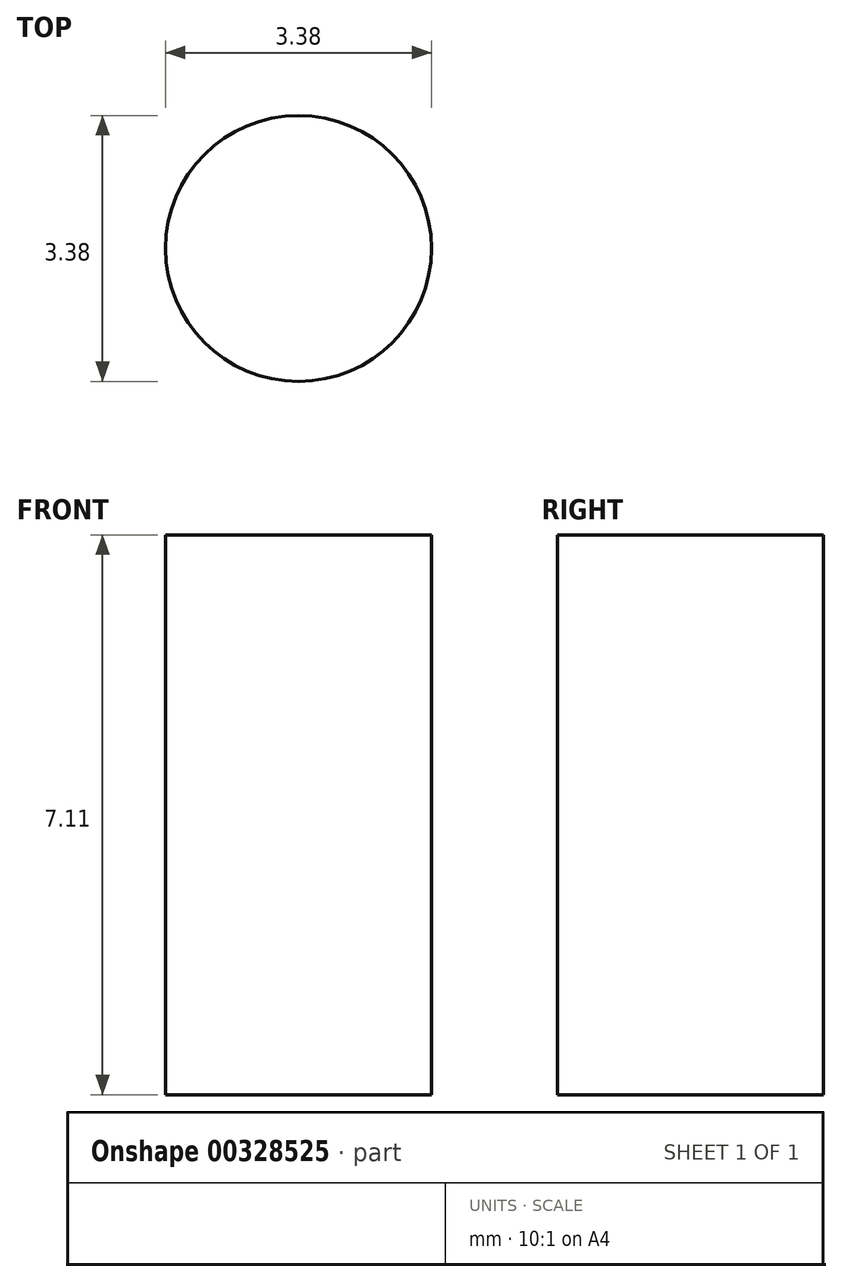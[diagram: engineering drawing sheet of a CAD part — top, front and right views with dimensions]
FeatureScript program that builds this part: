
annotation { "Feature Type Name" : "Feature", "Feature Type Description" : "" }
export const myFeature = defineFeature(function(context is Context, id is Id, definition is map)
    precondition{}
    {
        {
            var Q0;
            Q0=qCreatedBy(makeId("Top.planeOp"),FACE);
            var sketch = newSketch(context, id + "F0", { "sketchPlane" : qUnion([Q0])});
            skCircle(sketch, "E0", {"center": v(0, 0) * mm, "radius": 1.69 * mm});
            skSolve(sketch);
        }
        {
            var Q0;
            Q0 = qSketchRegion(id + "F0", true);
            var Q1;
            Q1=makeQuery(id+"F0.imprint","IMPRINT",FACE,{"disambiguationData":[TD([[makeQuery(id+"F0.imprint","IMPRINT",EDGE,{"derivedFrom":sQuery(id+"F0.wireOp",EDGE,"E0")}),1.0]])]});
            extrude(context, id + "F1", {"entities" : qUnion([Q0, Q1]), "depth" : 7.11 * mm});
        }
    });
